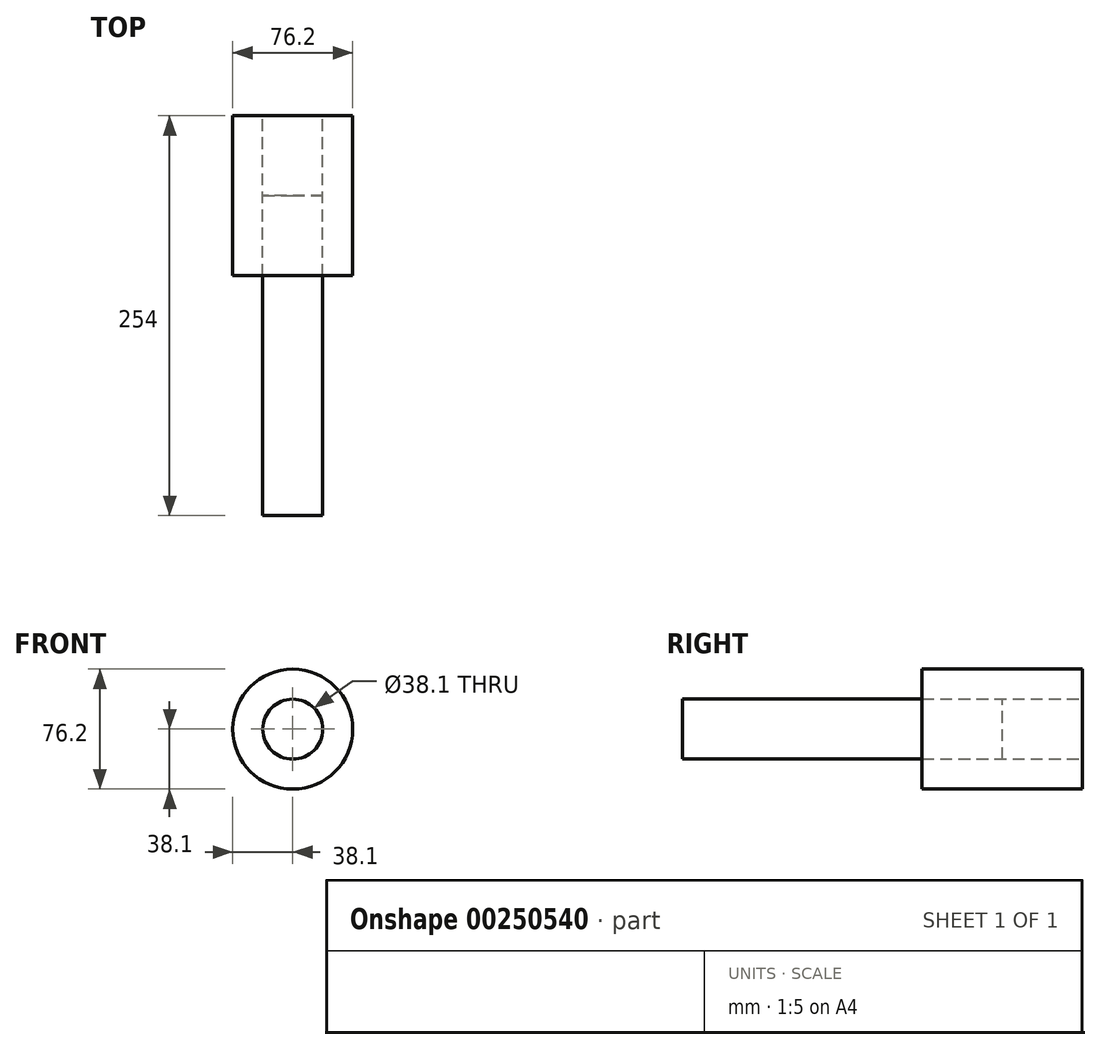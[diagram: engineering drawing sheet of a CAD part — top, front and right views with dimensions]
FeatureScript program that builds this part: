
annotation { "Feature Type Name" : "Feature", "Feature Type Description" : "" }
export const myFeature = defineFeature(function(context is Context, id is Id, definition is map)
    precondition{}
    {
        {
            var Q0;
            Q0=qCreatedBy(makeId("Front.planeOp"),FACE);
            var sketch = newSketch(context, id + "F0", { "sketchPlane" : qUnion([Q0])});
            skCircle(sketch, "E0", {"center": v(0, 0) * mm, "radius": 38.1 * mm});
            skCircle(sketch, "E1", {"center": v(0, 0) * mm, "radius": 19.05 * mm});
            skSolve(sketch);
        }
        {
            var Q0;
            Q0 = qSketchRegion(id + "F0", true);
            extrude(context, id + "F1", {"entities" : qUnion([Q0]), "endBound" : BoundingType.SYMMETRIC, "depth" : 101.6 * mm});
        }
        {
            var Q0;
            Q0=makeQuery(id+"F0.imprint","IMPRINT",FACE,{"disambiguationData":[TD([[makeQuery(id+"F0.imprint","IMPRINT",EDGE,{"derivedFrom":sQuery(id+"F0.wireOp",EDGE,"E1")}),1.0]])]});
            extrude(context, id + "F2", {"entities" : qUnion([Q0]), "depth" : 203.2 * mm});
        }
    });
